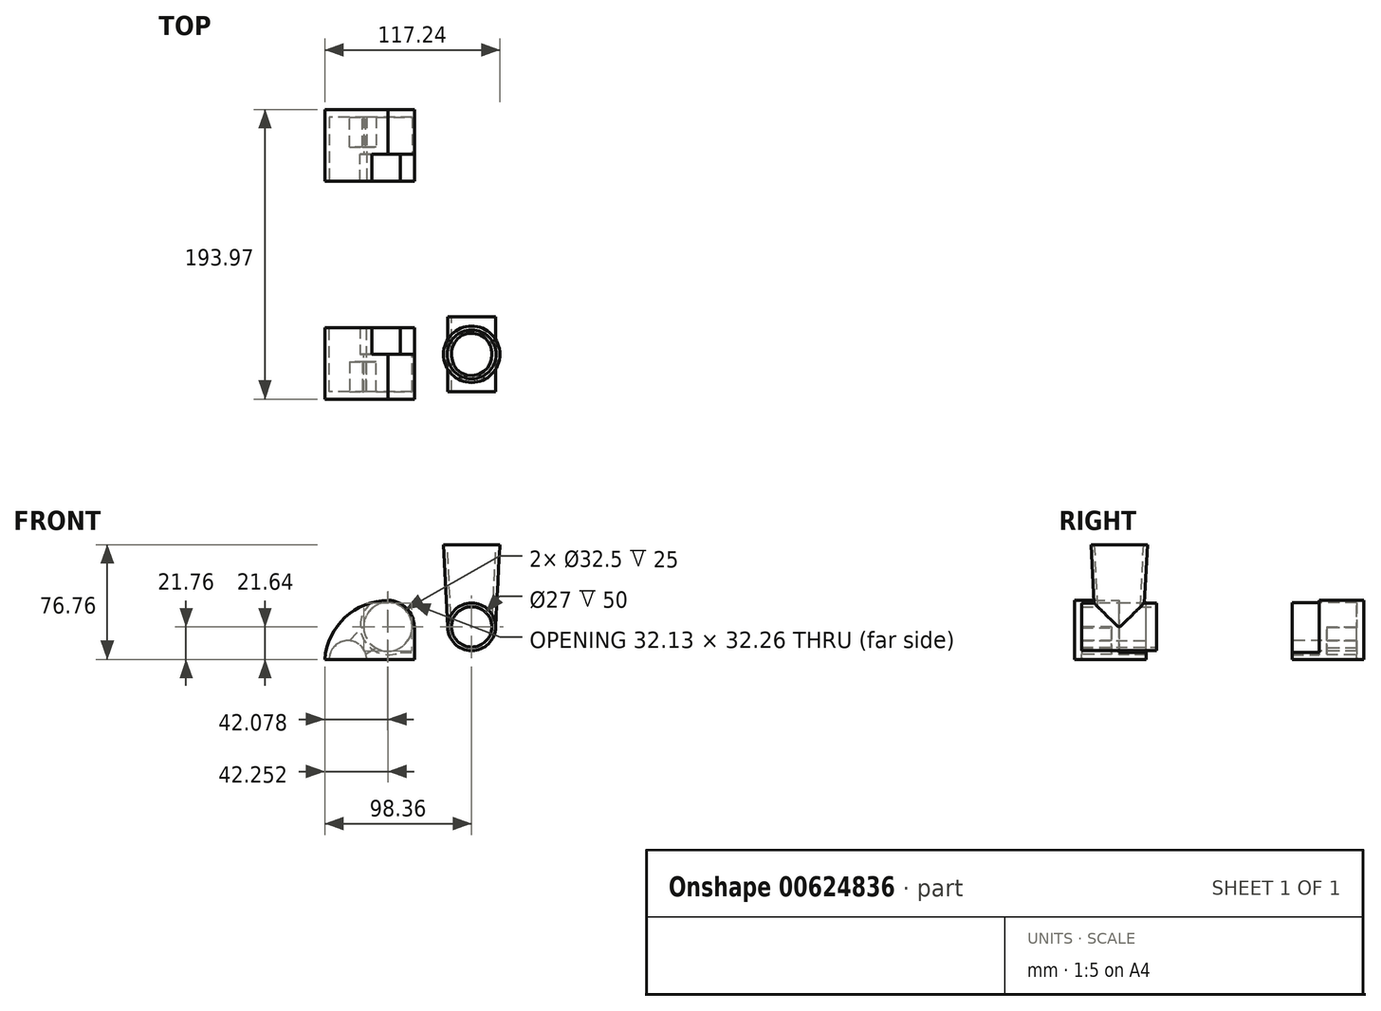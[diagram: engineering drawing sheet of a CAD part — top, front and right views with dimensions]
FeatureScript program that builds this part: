
annotation { "Feature Type Name" : "Feature", "Feature Type Description" : "" }
export const myFeature = defineFeature(function(context is Context, id is Id, definition is map)
    precondition{}
    {
        {
            var Q0;
            Q0=qCreatedBy(makeId("Top.planeOp"),FACE);
            var sketch = newSketch(context, id + "F0", { "sketchPlane" : qUnion([Q0])});
            skCircle(sketch, "E0", {"center": v(0, 0) * mm, "radius": 16 * mm});
            skSolve(sketch);
        }
        {
            var Q0;
            Q0=makeQuery(id+"F0.imprint","IMPRINT",FACE,{"disambiguationData":[TD([[makeQuery(id+"F0.imprint","IMPRINT",EDGE,{"derivedFrom":sQuery(id+"F0.wireOp",EDGE,"E0")}),1.0]])]});
            extrude(context, id + "F1", {"entities" : qUnion([Q0]), "depth" : 55 * mm, "offsetDistance" : 25 * mm, "hasDraft" : true, "draftAngle" : 3 * degree});
        }
        {
            var Q0;
            Q0=qCreatedBy(makeId("Front.planeOp"),FACE);
            var sketch = newSketch(context, id + "F2", { "sketchPlane" : qUnion([Q0])});
            skCircle(sketch, "E1", {"center": v(0, 0) * mm, "radius": 16 * mm});
            skSolve(sketch);
        }
        {
            var Q0;
            Q0=makeQuery(id+"F2.imprint","IMPRINT",FACE,{"disambiguationData":[TD([[makeQuery(id+"F2.imprint","IMPRINT",EDGE,{"derivedFrom":sQuery(id+"F2.wireOp",EDGE,"E1")}),1.0]])]});
            extrude(context, id + "F3", {"entities" : qUnion([Q0]), "operationType" : NewBodyOperationType.ADD, "endBound" : BoundingType.SYMMETRIC, "depth" : 50 * mm, "offsetDistance" : 25 * mm});
        }
        {
            var Q0;
            Q0=makeQuery(id+"F3.opExtrude","CAP_FACE",FACE,{"disambiguationData":[OSD([sQuery(id+"F2.wireOp",EDGE,"E1")])],"isStart":false});
            var Q1;
            Q1=makeQuery(id+"F3.opExtrude","CAP_FACE",FACE,{"disambiguationData":[OSD([sQuery(id+"F2.wireOp",EDGE,"E1")])],"isStart":true});
            var Q2;
            Q2=makeQuery(id+"F1.opExtrude","CAP_FACE",FACE,{"disambiguationData":[OSD([sQuery(id+"F0.wireOp",EDGE,"E0")])],"isStart":false});
            shell(context, id + "F4", {"entities" : qUnion([Q0, Q1, Q2]), "thickness" : 2.5 * mm});
        }
        {
            var Q0;
            Q0=qCreatedBy(makeId("Front.planeOp"),FACE);
            var sketch = newSketch(context, id + "F5", { "sketchPlane" : qUnion([Q0])});
            skCircle(sketch, "E2", {"center": v(-56.1, 0) * mm, "radius": 16.25 * mm});
            skCircle(sketch, "E3.0", {"center": v(-56.1, 0) * mm, "radius": 17.75 * mm});
            skLineSegment(sketch, "E4.bottom", {"start": v(-38.36, 17.75) * mm, "end": v(-98.36, 17.75) * mm});
            skLineSegment(sketch, "E4.top", {"start": v(-38.36, -21.76) * mm, "end": v(-98.36, -21.76) * mm});
            skLineSegment(sketch, "E4.left", {"start": v(-38.36, 17.75) * mm, "end": v(-38.36, -21.76) * mm});
            skLineSegment(sketch, "E4.right", {"start": v(-98.36, 17.75) * mm, "end": v(-98.36, -21.76) * mm});
            skArc(sketch, "E5", {"start": v(-70.36, -21.76) * mm, "mid": v(-82.86, -9.26) * mm, "end": v(-95.36, -21.76) * mm});
            skSolve(sketch);
        }
        {
            var Q0;
            Q0=makeQuery(id+"F5.imprint","IMPRINT",FACE,{"disambiguationData":[TD([[makeQuery(id+"F5.imprint","IMPRINT",EDGE,{"derivedFrom":sQuery(id+"F5.wireOp",EDGE,"E2")}),-1.0]])]});
            var Q1;
            {var subQ4=sQuery(id+"F5.wireOp",EDGE,"E4.right");Q1=makeQuery(id+"F5.imprint","IMPRINT",FACE,{"disambiguationData":[TD([[makeQuery(id+"F5.imprint","IMPRINT",EDGE,{"derivedFrom":subQ4}),1.0]])]});}
            extrude(context, id + "F6", {"entities" : qUnion([Q0, Q1]), "depth" : 25 * mm, "offsetDistance" : 25 * mm});
        }
        {
            var Q0;
            Q0=makeQuery(id+"F6.opExtrude","CAP_FACE",FACE,{"disambiguationData":[OSD([sQuery(id+"F5.wireOp",EDGE,"E2"),sQuery(id+"F5.wireOp",EDGE,"E3.0"),sQuery(id+"F5.wireOp",EDGE,"E4.bottom"),sQuery(id+"F5.wireOp",EDGE,"E4.top"),sQuery(id+"F5.wireOp",EDGE,"E4.left"),sQuery(id+"F5.wireOp",EDGE,"E4.right"),sQuery(id+"F5.wireOp",EDGE,"E5")])],"isStart":false});
            var sketch = newSketch(context, id + "F7", { "sketchPlane" : qUnion([Q0])});
            skLineSegment(sketch, "E6", {"start": v(-85.94, -13.68) * mm, "end": v(-73.01, 0) * mm});
            skLineSegment(sketch, "E7", {"start": v(-73.01, 0) * mm, "end": v(-60.19, -12.12) * mm});
            skLineSegment(sketch, "E8", {"start": v(-60.19, -12.12) * mm, "end": v(-85.94, -27.69) * mm});
            skLineSegment(sketch, "E9", {"start": v(-85.94, -27.69) * mm, "end": v(-85.94, -13.68) * mm});
            skArc(sketch, "E10", {"start": v(-65.28, -15.2) * mm, "mid": v(-40.87, 9.1) * mm, "end": v(-73.83, -0.87) * mm});
            skLineSegment(sketch, "E11", {"start": v(-56.1, 17.75) * mm, "end": v(-98.36, 17.75) * mm});
            skLineSegment(sketch, "E12", {"start": v(-98.36, 17.75) * mm, "end": v(-98.36, -21.76) * mm});
            skLineSegment(sketch, "E13", {"start": v(-98.36, -21.76) * mm, "end": v(-38.36, -21.76) * mm});
            skLineSegment(sketch, "E14", {"start": v(-38.36, -21.76) * mm, "end": v(-38.36, 0) * mm});
            skSolve(sketch);
        }
        {
            var Q0;
            {var subQ0=sQuery(id+"F7.wireOp",EDGE,"E7");Q0=makeQuery(id+"F7.imprint","IMPRINT",FACE,{"disambiguationData":[TD([[makeQuery(id+"F7.imprint","IMPRINT",EDGE,{"derivedFrom":subQ0}),-1.0]])]});}
            var Q1;
            {var subQ0=sQuery(id+"F7.wireOp",EDGE,"E6");var subQ1=makeQuery(id+"F6.opExtrude","CAP_EDGE",EDGE,{"disambiguationData":[OSD([sQuery(id+"F5.wireOp",EDGE,"E5")])],"isStart":false});var subQ2=makeQuery(id+"F7.imprint","INTERSECT",VERTEX,{"derivedFrom":[subQ1,subQ0]});Q1=makeQuery(id+"F7.imprint","IMPRINT",FACE,{"disambiguationData":[TD([[makeQuery(id+"F7.imprint","IMPRINT",EDGE,{"disambiguationData":[TD([[subQ2,-1.0]])],"derivedFrom":subQ0}),-1.0]])]});}
            var Q2;
            {var subQ0=sQuery(id+"F7.wireOp",EDGE,"E9");Q2=makeQuery(id+"F7.imprint","IMPRINT",FACE,{"disambiguationData":[TD([[makeQuery(id+"F7.imprint","IMPRINT",EDGE,{"derivedFrom":subQ0}),-1.0]])]});}
            extrude(context, id + "F8", {"entities" : qUnion([Q0, Q1, Q2]), "operationType" : NewBodyOperationType.REMOVE, "oppositeDirection" : true, "depth" : 20 * mm, "offsetDistance" : 25 * mm});
        }
        {
            var Q0;
            Q0=makeQuery(id+"F6.opExtrude","CAP_FACE",FACE,{"disambiguationData":[OSD([sQuery(id+"F5.wireOp",EDGE,"E2"),sQuery(id+"F5.wireOp",EDGE,"E3.0"),sQuery(id+"F5.wireOp",EDGE,"E4.bottom"),sQuery(id+"F5.wireOp",EDGE,"E4.top"),sQuery(id+"F5.wireOp",EDGE,"E4.left"),sQuery(id+"F5.wireOp",EDGE,"E4.right"),sQuery(id+"F5.wireOp",EDGE,"E5")])],"isStart":true});
            var sketch = newSketch(context, id + "F9", { "sketchPlane" : qUnion([Q0])});
            skLineSegment(sketch, "E15", {"start": v(64.43, 17.75) * mm, "end": v(98.36, 17.75) * mm});
            skLineSegment(sketch, "E16", {"start": v(98.36, 17.75) * mm, "end": v(98.36, -21.76) * mm});
            skLineSegment(sketch, "E17", {"start": v(98.36, -21.76) * mm, "end": v(95.36, -21.76) * mm});
            skArc(sketch, "E18", {"start": v(95.36, -21.76) * mm, "mid": v(86.28, -9.74) * mm, "end": v(72.23, -15.18) * mm});
            skLineSegment(sketch, "E19", {"start": v(47.7, -17.16) * mm, "end": v(38.36, -17.16) * mm});
            skLineSegment(sketch, "E20", {"start": v(38.36, -17.16) * mm, "end": v(38.36, -21.76) * mm});
            skLineSegment(sketch, "E21", {"start": v(38.36, -21.76) * mm, "end": v(70.36, -21.76) * mm});
            skArc(sketch, "E22", {"start": v(72.23, -15.18) * mm, "mid": v(70.87, -18.35) * mm, "end": v(70.36, -21.76) * mm});
            skArc(sketch, "E23", {"start": v(47.7, -17.16) * mm, "mid": v(72.68, -7.67) * mm, "end": v(64.43, 17.75) * mm});
            skPoint(sketch, "E24.end.orphan", {"position": v(75.38, 0) * mm});
            skSolve(sketch);
        }
        {
            var Q0;
            Q0=makeQuery(id+"F9.imprint","IMPRINT",FACE,{"disambiguationData":[TD([[makeQuery(id+"F9.imprint","IMPRINT",EDGE,{"derivedFrom":sQuery(id+"F9.wireOp",EDGE,"E15")}),-1.0]])]});
            extrude(context, id + "F10", {"entities" : qUnion([Q0]), "operationType" : NewBodyOperationType.ADD, "depth" : 18 * mm, "offsetDistance" : 25 * mm});
        }
        {
            var Q0;
            {var subQ8=sQuery(id+"F7.wireOp",EDGE,"E10");Q0=makeQuery(id+"F7.imprint","IMPRINT",FACE,{"disambiguationData":[TD([[makeQuery(id+"F7.imprint","IMPRINT",EDGE,{"derivedFrom":subQ8}),-1.0]])]});}
            var Q1;
            {var subQ1=sQuery(id+"F7.wireOp",EDGE,"E6");var subQ5=sQuery(id+"F7.wireOp",EDGE,"E10");var subQ6=makeQuery(id+"F7.imprint","INTERSECT",VERTEX,{"derivedFrom":[subQ1,subQ5]});Q1=makeQuery(id+"F7.imprint","IMPRINT",FACE,{"disambiguationData":[TD([[makeQuery(id+"F7.imprint","IMPRINT",EDGE,{"disambiguationData":[TD([[subQ6,1.0]])],"derivedFrom":subQ1}),-1.0]])]});}
            var Q2;
            {var subQ0=sQuery(id+"F7.wireOp",EDGE,"E8");var subQ1=sQuery(id+"F7.wireOp",EDGE,"E7");var subQ2=makeQuery(id+"F7.imprint","INTERSECT",VERTEX,{"derivedFrom":[subQ1,subQ0]});Q2=makeQuery(id+"F7.imprint","IMPRINT",FACE,{"disambiguationData":[TD([[makeQuery(id+"F7.imprint","IMPRINT",EDGE,{"disambiguationData":[TD([[subQ2,1.0]])],"derivedFrom":subQ1}),1.0]])]});}
            var Q3;
            {var subQ0=sQuery(id+"F7.wireOp",EDGE,"E8");var subQ1=sQuery(id+"F7.wireOp",EDGE,"E7");var subQ2=makeQuery(id+"F7.imprint","INTERSECT",VERTEX,{"derivedFrom":[subQ1,subQ0]});Q3=makeQuery(id+"F7.imprint","IMPRINT",FACE,{"disambiguationData":[TD([[makeQuery(id+"F7.imprint","IMPRINT",EDGE,{"disambiguationData":[TD([[subQ2,1.0]])],"derivedFrom":subQ1}),-1.0]])]});}
            var Q4;
            {var subQ0=sQuery(id+"F7.wireOp",EDGE,"E10");Q4=makeQuery(id+"F7.imprint","IMPRINT",FACE,{"disambiguationData":[TD([[makeQuery(id+"F7.imprint","IMPRINT",EDGE,{"derivedFrom":subQ0}),1.0]])]});}
            var Q5;
            {var subQ3=sQuery(id+"F7.wireOp",EDGE,"E9");var subQ5=sQuery(id+"F7.wireOp",EDGE,"E6");var subQ6=makeQuery(id+"F7.imprint","INTERSECT",VERTEX,{"derivedFrom":[subQ5,subQ3]});Q5=makeQuery(id+"F7.imprint","IMPRINT",FACE,{"disambiguationData":[TD([[makeQuery(id+"F7.imprint","IMPRINT",EDGE,{"disambiguationData":[TD([[subQ6,-1.0]])],"derivedFrom":subQ5}),-1.0]])]});}
            var Q6;
            {var subQ0=sQuery(id+"F7.wireOp",EDGE,"E9");var subQ1=sQuery(id+"F7.wireOp",EDGE,"E6");var subQ2=makeQuery(id+"F7.imprint","INTERSECT",VERTEX,{"derivedFrom":[subQ1,subQ0]});Q6=makeQuery(id+"F7.imprint","IMPRINT",FACE,{"disambiguationData":[TD([[makeQuery(id+"F7.imprint","IMPRINT",EDGE,{"disambiguationData":[TD([[subQ2,-1.0]])],"derivedFrom":subQ1}),1.0]])]});}
            var Q7;
            {var subQ0=sQuery(id+"F7.wireOp",EDGE,"E13");var subQ1=sQuery(id+"F7.wireOp",EDGE,"E8");var subQ2=makeQuery(id+"F7.imprint","INTERSECT",VERTEX,{"derivedFrom":[subQ1,subQ0]});Q7=makeQuery(id+"F7.imprint","IMPRINT",FACE,{"disambiguationData":[TD([[makeQuery(id+"F7.imprint","IMPRINT",EDGE,{"disambiguationData":[TD([[subQ2,1.0]])],"derivedFrom":subQ1}),1.0]])]});}
            extrude(context, id + "F11", {"entities" : qUnion([Q0, Q1, Q2, Q3, Q4, Q5, Q6, Q7]), "operationType" : NewBodyOperationType.ADD, "depth" : 5 * mm, "offsetDistance" : 25 * mm});
        }
        {
            var Q0;
            Q0=makeQuery(id+"F11.boolean.opBoolean","MERGE",EDGE,{"derivedFrom":[makeQuery(id+"F10.boolean.opBoolean","MERGE",EDGE,{"derivedFrom":[makeQuery(id+"F6.opExtrude","SWEPT_EDGE",EDGE,{"disambiguationData":[OSD([sQuery(id+"F5.wireOp",EDGE,"E4.bottom"),sQuery(id+"F5.wireOp",EDGE,"E4.right")])]}),makeQuery(id+"F10.opExtrude","SWEPT_EDGE",EDGE,{"disambiguationData":[OSD([sQuery(id+"F9.wireOp",EDGE,"E15"),sQuery(id+"F9.wireOp",EDGE,"E16")])]})]}),makeQuery(id+"F11.opExtrude","SWEPT_EDGE",EDGE,{"disambiguationData":[OSD([sQuery(id+"F7.wireOp",EDGE,"E11"),sQuery(id+"F7.wireOp",EDGE,"E12")])]})]});
            fillet(context, id + "F12", {"entities" : qUnion([Q0]), "radius" : 42.83 * mm, "tangentPropagation" : true, "allowEdgeOverflow" : false});
        }
        {
            var Q0;
            Q0=qCreatedBy(makeId("Front.planeOp"),FACE);
            cPlane(context, id + "F13", {"entities" : qUnion([Q0]), "cplaneType" : CPlaneType.OFFSET, "offset" : 66.99 * mm, "oppositeDirection" : true, "width" : 150 * mm, "height" : 150 * mm});
        }
        {
            var Q0;
            Q0=makeQuery(id+"F6.opExtrude","SWEPT_BODY",BODY,{"disambiguationData":[OSD([sQuery(id+"F5.wireOp",EDGE,"E2"),sQuery(id+"F5.wireOp",EDGE,"E3.0"),sQuery(id+"F5.wireOp",EDGE,"E4.bottom"),sQuery(id+"F5.wireOp",EDGE,"E4.top"),sQuery(id+"F5.wireOp",EDGE,"E4.left"),sQuery(id+"F5.wireOp",EDGE,"E4.right"),sQuery(id+"F5.wireOp",EDGE,"E5")])]});
            var Q1;
            Q1=qCreatedBy(id+"F13.planeOp",FACE);
            mirror(context, id + "F14", {"entities" : qUnion([Q0]), "mirrorPlane" : qUnion([Q1])});
        }
    });
